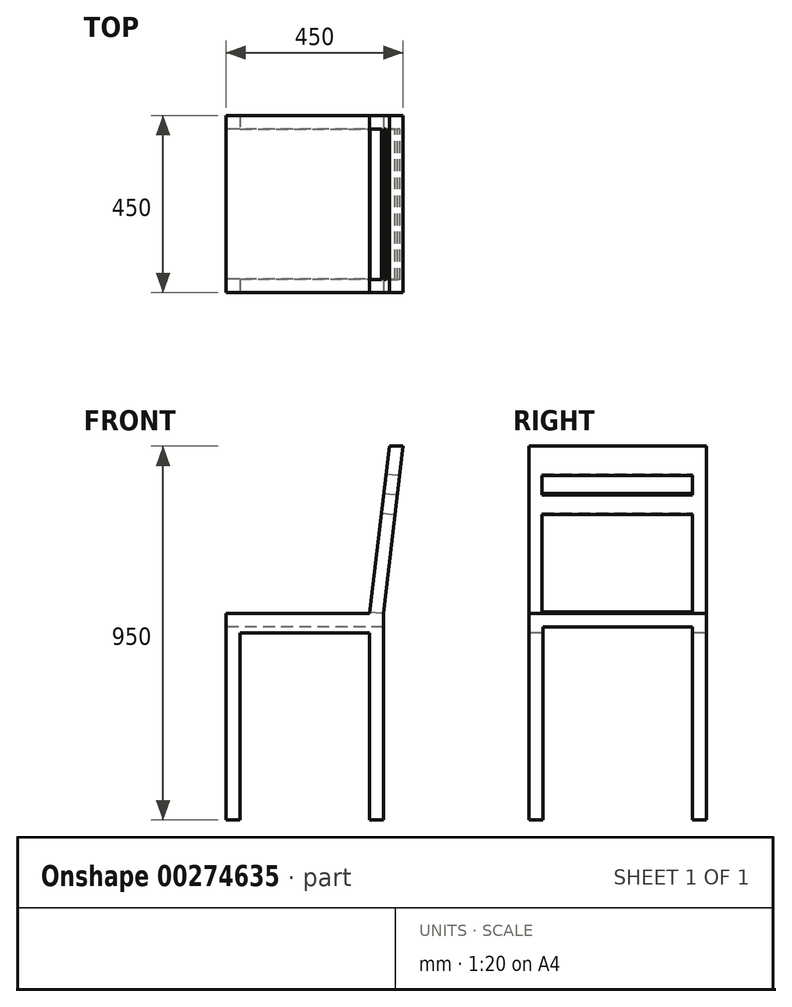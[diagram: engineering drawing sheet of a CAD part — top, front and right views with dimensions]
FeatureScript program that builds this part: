
annotation { "Feature Type Name" : "Feature", "Feature Type Description" : "" }
export const myFeature = defineFeature(function(context is Context, id is Id, definition is map)
    precondition{}
    {
        {
            var Q0;
            Q0=qCreatedBy(makeId("Top.planeOp"),FACE);
            var sketch = newSketch(context, id + "F0", { "sketchPlane" : qUnion([Q0])});
            skLineSegment(sketch, "E0.bottom", {"start": v(225, 225) * mm, "end": v(-225, 225) * mm});
            skLineSegment(sketch, "E0.top", {"start": v(225, -225) * mm, "end": v(-225, -225) * mm});
            skLineSegment(sketch, "E0.left", {"start": v(225, 225) * mm, "end": v(225, -225) * mm});
            skLineSegment(sketch, "E0.right", {"start": v(-225, 225) * mm, "end": v(-225, -225) * mm});
            skPoint(sketch, "E0.middle", {"position": v(0, 0) * mm});
            skSolve(sketch);
        }
        {
            var Q0;
            Q0=qSketchRegion(id+"F0",true);
            extrude(context, id + "F1", {"entities" : qUnion([Q0]), "depth" : 950 * mm});
        }
        {
            var Q0;
            Q0=makeQuery(id+"F1.opExtrude","SWEPT_FACE",FACE,{"disambiguationData":[OSD([sQuery(id+"F0.wireOp",EDGE,"E0.top")])]});
            var sketch = newSketch(context, id + "F2", { "sketchPlane" : qUnion([Q0])});
            skLineSegment(sketch, "E1.bottom", {"start": v(225, 475) * mm, "end": v(-225, 475) * mm});
            skLineSegment(sketch, "E1.top", {"start": v(225, 525) * mm, "end": v(-225, 525) * mm});
            skLineSegment(sketch, "E1.left", {"start": v(225, 475) * mm, "end": v(225, 525) * mm});
            skLineSegment(sketch, "E1.right", {"start": v(-225, 475) * mm, "end": v(-225, 525) * mm});
            skLineSegment(sketch, "E2", {"start": v(175, 525) * mm, "end": v(225, 950) * mm});
            skLineSegment(sketch, "E3", {"start": v(139.76, 525) * mm, "end": v(189.76, 950) * mm});
            skLineSegment(sketch, "E4", {"start": v(139.76, 525) * mm, "end": v(139.76, 0) * mm});
            skLineSegment(sketch, "E5", {"start": v(175, 525) * mm, "end": v(175, 0) * mm});
            skLineSegment(sketch, "E6", {"start": v(-225, 475) * mm, "end": v(-225, 0) * mm});
            skLineSegment(sketch, "E7", {"start": v(-190, 475) * mm, "end": v(-190, 0) * mm});
            skSolve(sketch);
        }
        {
            var Q0;
            {var subQ4=sQuery(id+"F2.wireOp",EDGE,"E3");Q0=makeQuery(id+"F2.imprint","IMPRINT",FACE,{"disambiguationData":[TD([[makeQuery(id+"F2.imprint","IMPRINT",EDGE,{"derivedFrom":subQ4}),1.0]])]});}
            var Q1;
            {var subQ0=sQuery(id+"F2.wireOp",EDGE,"E7");Q1=makeQuery(id+"F2.imprint","IMPRINT",FACE,{"disambiguationData":[TD([[makeQuery(id+"F2.imprint","IMPRINT",EDGE,{"derivedFrom":subQ0}),1.0]])]});}
            var Q2;
            {var subQ4=sQuery(id+"F2.wireOp",EDGE,"E2");Q2=makeQuery(id+"F2.imprint","IMPRINT",FACE,{"disambiguationData":[TD([[makeQuery(id+"F2.imprint","IMPRINT",EDGE,{"derivedFrom":subQ4}),-1.0]])]});}
            var Q3;
            {var subQ0=sQuery(id+"F2.wireOp",EDGE,"E1.left");Q3=makeQuery(id+"F2.imprint","IMPRINT",FACE,{"disambiguationData":[TD([[makeQuery(id+"F2.imprint","IMPRINT",EDGE,{"derivedFrom":subQ0}),-1.0]])]});}
            var Q4;
            {var subQ1=sQuery(id+"F0.wireOp",EDGE,"E0.top");var subQ4=sQuery(id+"F2.wireOp",EDGE,"E5");var subQ6=makeQuery(id+"F1.opExtrude","CAP_EDGE",EDGE,{"disambiguationData":[OSD([subQ1])],"isStart":true});var subQ8=makeQuery(id+"F2.imprint","INTERSECT",VERTEX,{"derivedFrom":[subQ6,subQ4]});Q4=makeQuery(id+"F2.imprint","IMPRINT",FACE,{"disambiguationData":[TD([[makeQuery(id+"F2.imprint","IMPRINT",EDGE,{"disambiguationData":[TD([[subQ8,1.0]])],"derivedFrom":subQ4}),1.0]])]});}
            extrude(context, id + "F3", {"entities" : qUnion([Q0, Q1, Q2, Q3, Q4]), "operationType" : NewBodyOperationType.REMOVE, "endBound" : BoundingType.THROUGH_ALL, "oppositeDirection" : true, "depth" : 200 * mm});
        }
        {
            var Q0;
            Q0=makeQuery(id+"F1.opExtrude","SWEPT_FACE",FACE,{"disambiguationData":[OSD([sQuery(id+"F0.wireOp",EDGE,"E0.right")])]});
            var sketch = newSketch(context, id + "F4", { "sketchPlane" : qUnion([Q0])});
            skLineSegment(sketch, "E8.bottom", {"start": v(-190, 0) * mm, "end": v(190, 0) * mm});
            skLineSegment(sketch, "E8.top", {"start": v(-190, 490) * mm, "end": v(190, 490) * mm});
            skLineSegment(sketch, "E8.left", {"start": v(-190, 0) * mm, "end": v(-190, 490) * mm});
            skLineSegment(sketch, "E8.right", {"start": v(190, 0) * mm, "end": v(190, 490) * mm});
            skSolve(sketch);
        }
        {
            var Q0;
            Q0=makeQuery(id+"F4.imprint","IMPRINT",FACE,{"disambiguationData":[TD([[makeQuery(id+"F4.imprint","IMPRINT",EDGE,{"derivedFrom":sQuery(id+"F4.wireOp",EDGE,"E8.bottom")}),1.0]])]});
            extrude(context, id + "F5", {"entities" : qUnion([Q0]), "operationType" : NewBodyOperationType.REMOVE, "endBound" : BoundingType.THROUGH_ALL, "oppositeDirection" : true, "depth" : 25 * mm});
        }
        {
            var Q0;
            Q0=makeQuery(id+"F3.boolean.opBoolean","COPY",FACE,{"derivedFrom":makeQuery(id+"F3.opExtrude","SWEPT_FACE",FACE,{"disambiguationData":[OSD([sQuery(id+"F2.wireOp",EDGE,"E2")])]})});
            var sketch = newSketch(context, id + "F6", { "sketchPlane" : qUnion([Q0])});
            skLineSegment(sketch, "E9.bottom", {"start": v(-192.12, 894.78) * mm, "end": v(190.16, 894.78) * mm});
            skLineSegment(sketch, "E9.top", {"start": v(-192.12, 844.78) * mm, "end": v(190.16, 844.78) * mm});
            skLineSegment(sketch, "E9.left", {"start": v(-192.12, 894.78) * mm, "end": v(-192.12, 844.78) * mm});
            skLineSegment(sketch, "E9.right", {"start": v(190.16, 894.78) * mm, "end": v(190.16, 844.78) * mm});
            skLineSegment(sketch, "E10.bottom", {"start": v(-192.12, 794.78) * mm, "end": v(190.16, 794.78) * mm});
            skLineSegment(sketch, "E10.top", {"start": v(-192.12, 541.85) * mm, "end": v(190.16, 541.85) * mm});
            skLineSegment(sketch, "E10.left", {"start": v(-192.12, 794.78) * mm, "end": v(-192.12, 541.85) * mm});
            skLineSegment(sketch, "E10.right", {"start": v(190.16, 794.78) * mm, "end": v(190.16, 541.85) * mm});
            skSolve(sketch);
        }
        {
            var Q0;
            Q0=makeQuery(id+"F6.imprint","IMPRINT",FACE,{"disambiguationData":[TD([[makeQuery(id+"F6.imprint","IMPRINT",EDGE,{"derivedFrom":sQuery(id+"F6.wireOp",EDGE,"E9.bottom")}),-1.0]])]});
            var Q1;
            Q1=makeQuery(id+"F6.imprint","IMPRINT",FACE,{"disambiguationData":[TD([[makeQuery(id+"F6.imprint","IMPRINT",EDGE,{"derivedFrom":sQuery(id+"F6.wireOp",EDGE,"E10.bottom")}),-1.0]])]});
            extrude(context, id + "F7", {"entities" : qUnion([Q0, Q1]), "operationType" : NewBodyOperationType.REMOVE, "endBound" : BoundingType.THROUGH_ALL, "oppositeDirection" : true, "depth" : 25 * mm});
        }
    });
